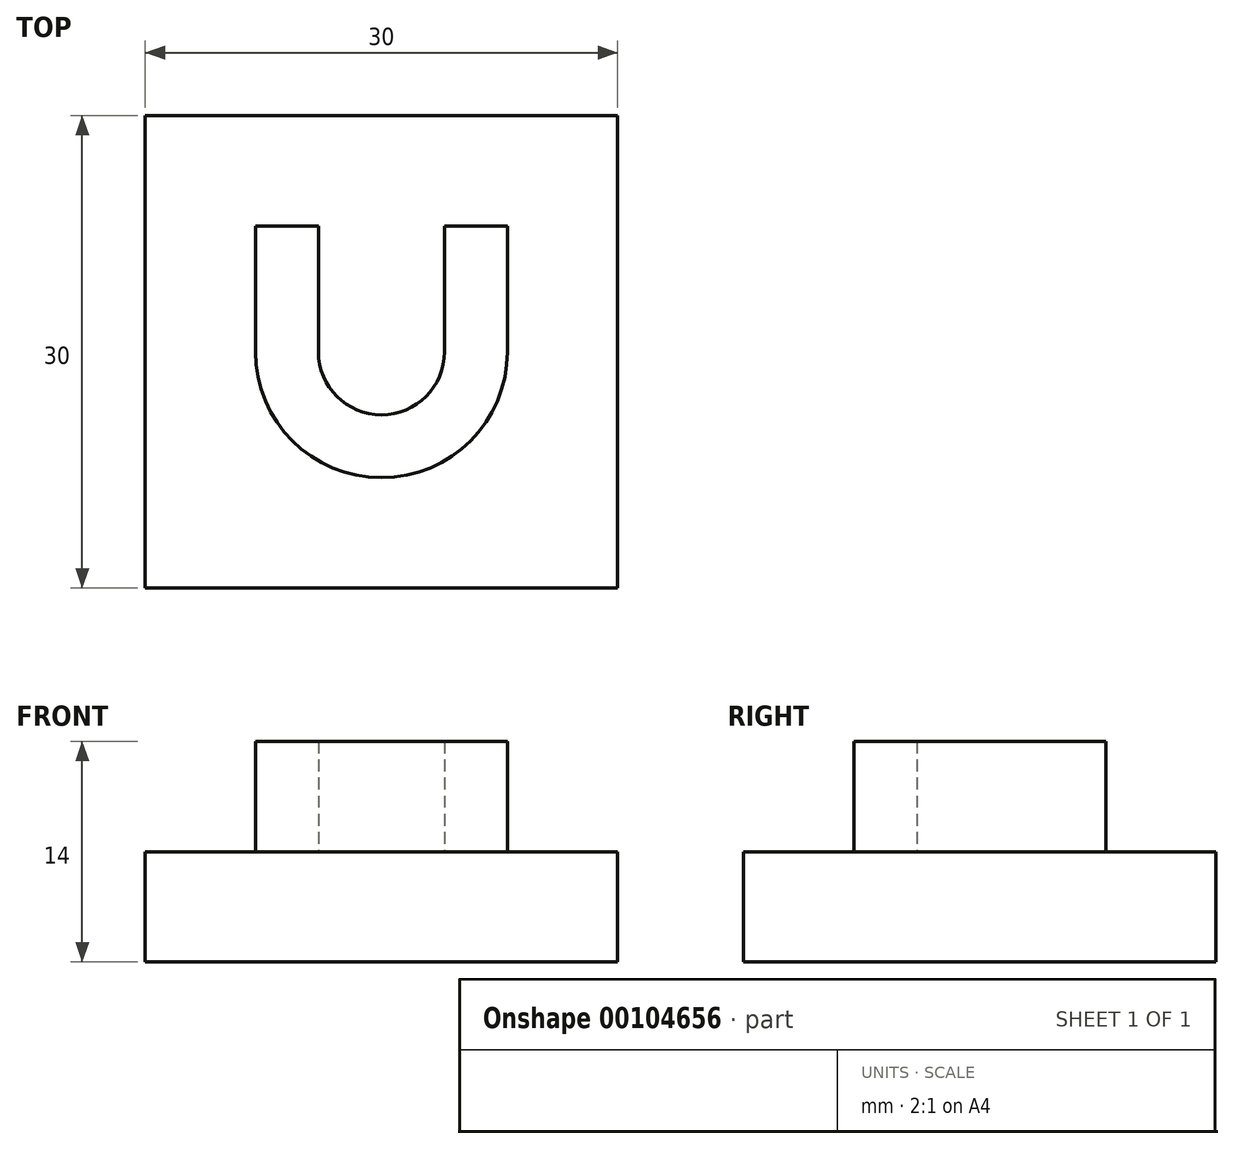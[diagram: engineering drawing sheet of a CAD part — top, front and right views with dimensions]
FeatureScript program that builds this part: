
annotation { "Feature Type Name" : "Feature", "Feature Type Description" : "" }
export const myFeature = defineFeature(function(context is Context, id is Id, definition is map)
    precondition{}
    {
        {
            var Q0;
            Q0=qCreatedBy(makeId("Top.planeOp"),FACE);
            var sketch = newSketch(context, id + "F0", { "sketchPlane" : qUnion([Q0])});
            skLineSegment(sketch, "E0.bottom", {"start": v(15, -15) * mm, "end": v(-15, -15) * mm});
            skLineSegment(sketch, "E0.top", {"start": v(15, 15) * mm, "end": v(-15, 15) * mm});
            skLineSegment(sketch, "E0.left", {"start": v(15, -15) * mm, "end": v(15, 15) * mm});
            skLineSegment(sketch, "E0.right", {"start": v(-15, -15) * mm, "end": v(-15, 15) * mm});
            skPoint(sketch, "E0.middle", {"position": v(0, 0) * mm});
            skSolve(sketch);
        }
        {
            var Q0;
            Q0=makeQuery(id+"F0.imprint","IMPRINT",FACE,{"disambiguationData":[TD([[makeQuery(id+"F0.imprint","IMPRINT",EDGE,{"derivedFrom":sQuery(id+"F0.wireOp",EDGE,"E0.bottom")}),-1.0]])]});
            extrude(context, id + "F1", {"entities" : qUnion([Q0]), "depth" : 7 * mm});
        }
        {
            var Q0;
            Q0=makeQuery(id+"F1.opExtrude","CAP_FACE",FACE,{"disambiguationData":[OSD([sQuery(id+"F0.wireOp",EDGE,"E0.bottom"),sQuery(id+"F0.wireOp",EDGE,"E0.top"),sQuery(id+"F0.wireOp",EDGE,"E0.left"),sQuery(id+"F0.wireOp",EDGE,"E0.right")])],"isStart":false});
            var sketch = newSketch(context, id + "F2", { "sketchPlane" : qUnion([Q0])});
            skLineSegment(sketch, "E1", {"start": v(-4, 0) * mm, "end": v(4, 0) * mm, "construction": true});
            skArc(sketch, "E2", {"start": v(-4, 0) * mm, "mid": v(0, -4) * mm, "end": v(4, 0) * mm});
            skArc(sketch, "E3.0", {"start": v(-8, 0) * mm, "mid": v(0, -8) * mm, "end": v(8, 0) * mm});
            skLineSegment(sketch, "E4", {"start": v(-4, 0) * mm, "end": v(-8, 0) * mm});
            skLineSegment(sketch, "E5", {"start": v(4, 0) * mm, "end": v(8, 0) * mm});
            skSolve(sketch);
        }
        {
            var Q0;
            Q0 = qSketchRegion(id + "F2", true);
            extrude(context, id + "F3", {"entities" : qUnion([Q0]), "operationType" : NewBodyOperationType.ADD, "depth" : 7 * mm});
        }
        {
            var Q0;
            Q0=makeQuery(id+"F3.opExtrude","SWEPT_FACE",FACE,{"disambiguationData":[OSD([sQuery(id+"F2.wireOp",EDGE,"E4")])]});
            var Q1;
            Q1=makeQuery(id+"F3.opExtrude","SWEPT_FACE",FACE,{"disambiguationData":[OSD([sQuery(id+"F2.wireOp",EDGE,"E5")])]});
            extrude(context, id + "F4", {"entities" : qUnion([Q0, Q1]), "operationType" : NewBodyOperationType.ADD, "depth" : 8 * mm});
        }
    });
